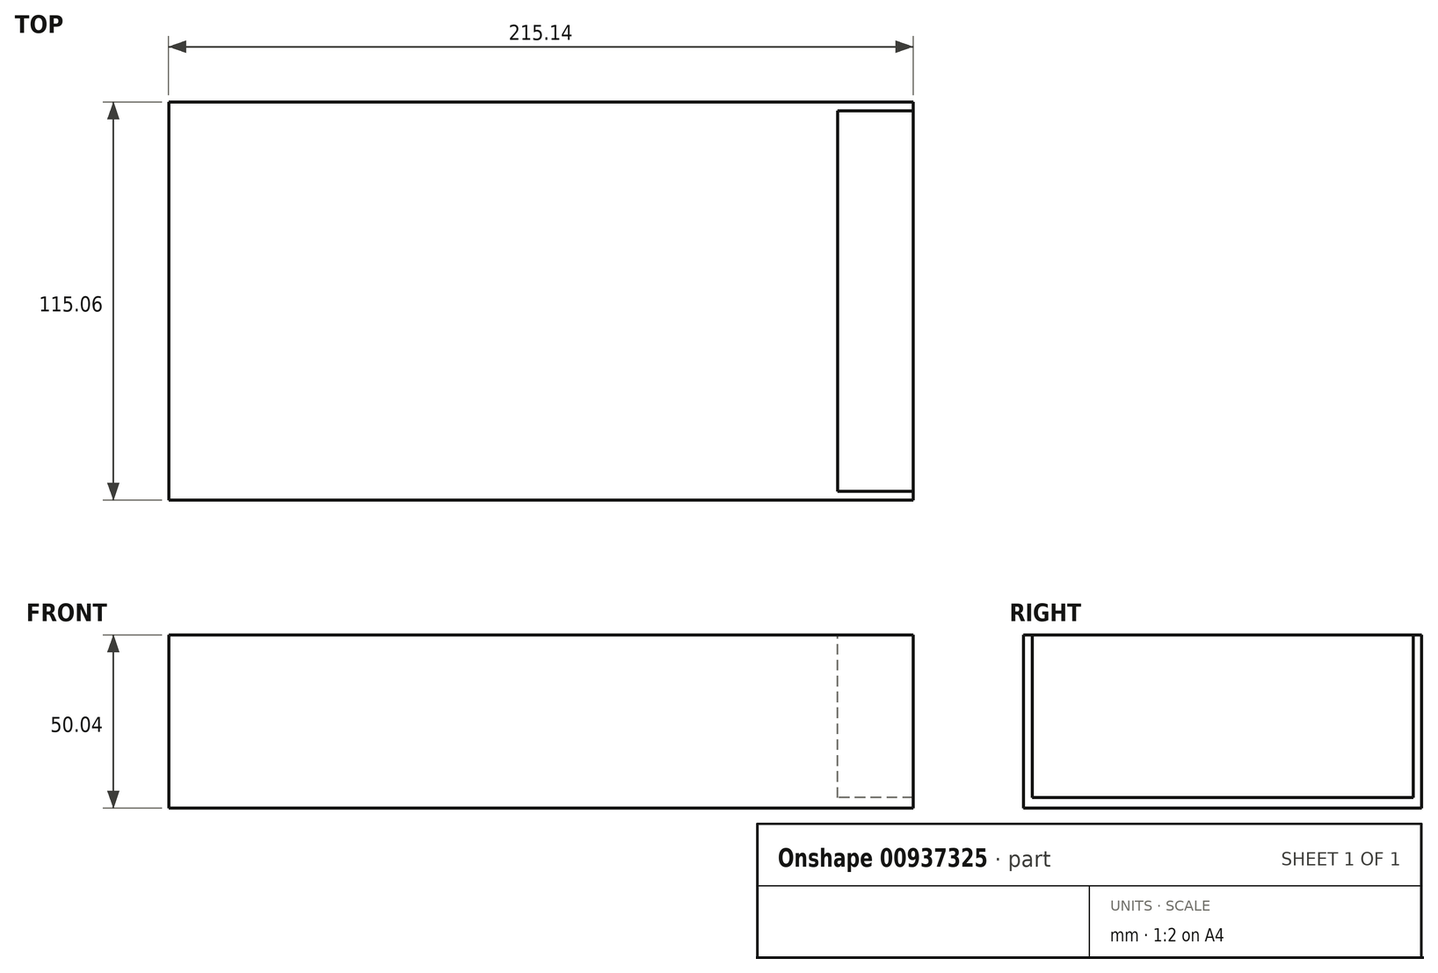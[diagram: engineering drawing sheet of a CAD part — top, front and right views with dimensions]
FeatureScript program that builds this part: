
annotation { "Feature Type Name" : "Feature", "Feature Type Description" : "" }
export const myFeature = defineFeature(function(context is Context, id is Id, definition is map)
    precondition{}
    {
        {
            var Q0;
            Q0=qCreatedBy(makeId("Top.planeOp"),FACE);
            var sketch = newSketch(context, id + "F0", { "sketchPlane" : qUnion([Q0])});
            skLineSegment(sketch, "E0.bottom", {"start": v(107.57, -57.53) * mm, "end": v(-107.57, -57.53) * mm});
            skLineSegment(sketch, "E0.top", {"start": v(107.57, 57.53) * mm, "end": v(-107.57, 57.53) * mm});
            skLineSegment(sketch, "E0.left", {"start": v(107.57, -57.53) * mm, "end": v(107.57, 57.53) * mm});
            skLineSegment(sketch, "E0.right", {"start": v(-107.57, -57.53) * mm, "end": v(-107.57, 57.53) * mm});
            skPoint(sketch, "E0.middle", {"position": v(0, 0) * mm});
            skSolve(sketch);
        }
        {
            var Q0;
            Q0 = qSketchRegion(id + "F0", true);
            extrude(context, id + "F1", {"entities" : qUnion([Q0]), "depth" : 50.04 * mm, "offsetDistance" : 25 * mm});
        }
        {
            var Q0;
            Q0=makeQuery(id+"F1.opExtrude","CAP_FACE",FACE,{"disambiguationData":[OSD([sQuery(id+"F0.wireOp",EDGE,"E0.bottom"),sQuery(id+"F0.wireOp",EDGE,"E0.top"),sQuery(id+"F0.wireOp",EDGE,"E0.left"),sQuery(id+"F0.wireOp",EDGE,"E0.right")])],"isStart":false});
            var sketch = newSketch(context, id + "F2", { "sketchPlane" : qUnion([Q0])});
            skLineSegment(sketch, "E1.bottom", {"start": v(107.57, 55.03) * mm, "end": v(85.72, 55.03) * mm});
            skLineSegment(sketch, "E1.top", {"start": v(107.57, -55.03) * mm, "end": v(85.72, -55.03) * mm});
            skLineSegment(sketch, "E1.left", {"start": v(107.57, 55.03) * mm, "end": v(107.57, -55.03) * mm});
            skLineSegment(sketch, "E1.right", {"start": v(85.72, 55.03) * mm, "end": v(85.72, -55.03) * mm});
            skLineSegment(sketch, "E2", {"start": v(-127.55, 0) * mm, "end": v(156.08, 0) * mm, "construction": true});
            skSolve(sketch);
        }
        {
            var Q0;
            Q0=makeQuery(id+"F2.imprint","IMPRINT",FACE,{"disambiguationData":[TD([[makeQuery(id+"F2.imprint","IMPRINT",EDGE,{"derivedFrom":sQuery(id+"F2.wireOp",EDGE,"E1.bottom")}),1.0]])]});
            extrude(context, id + "F3", {"entities" : qUnion([Q0]), "operationType" : NewBodyOperationType.REMOVE, "oppositeDirection" : true, "depth" : 47 * mm, "offsetDistance" : 25 * mm});
        }
    });
